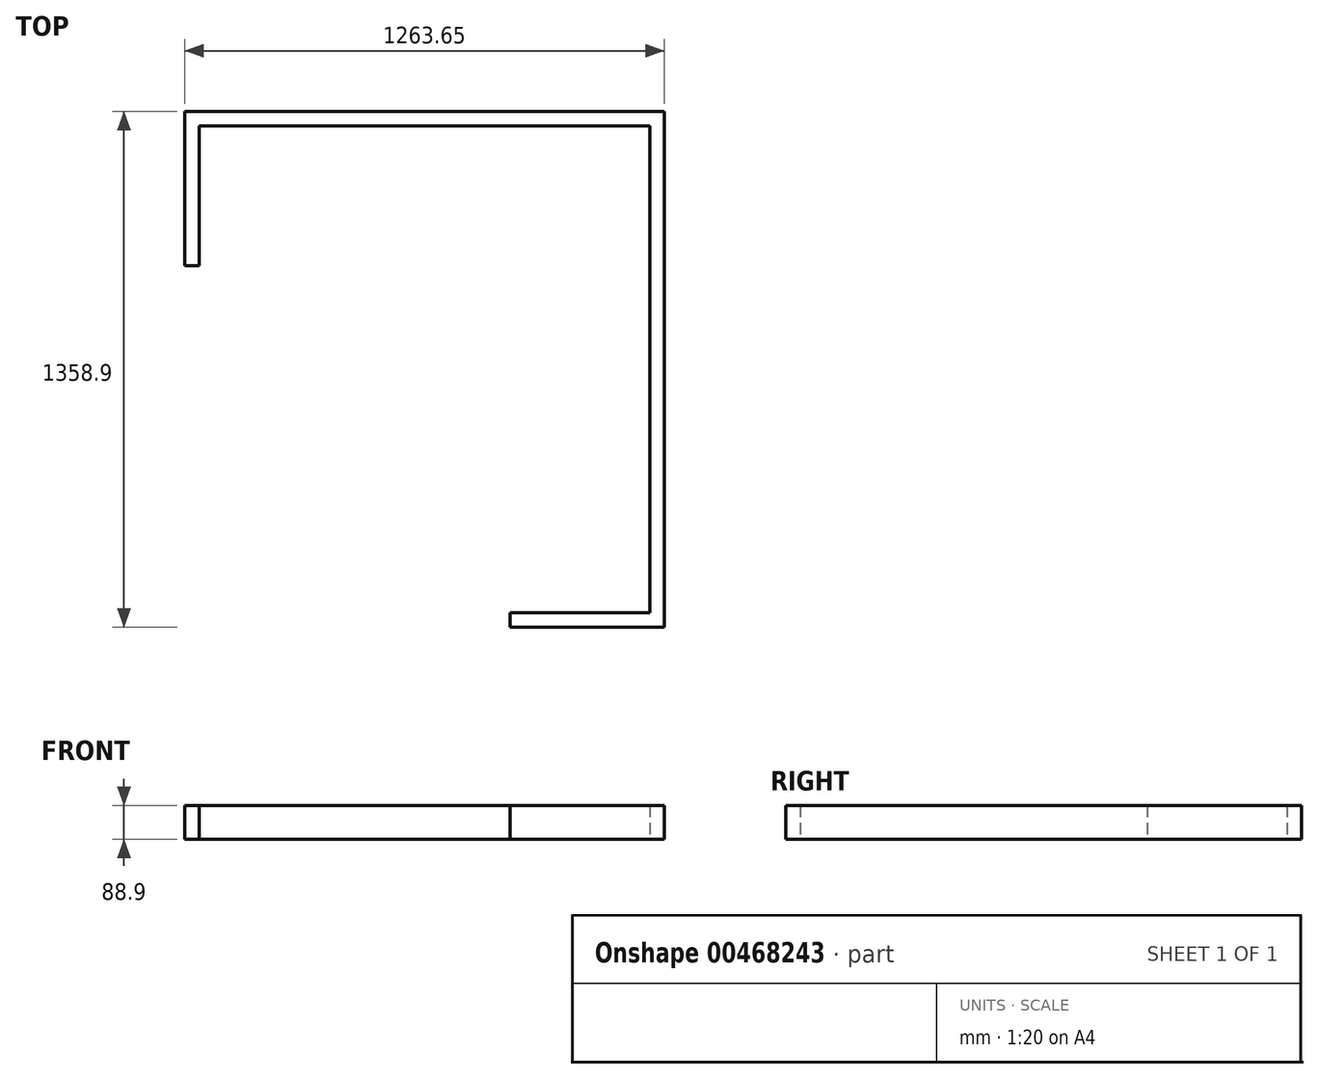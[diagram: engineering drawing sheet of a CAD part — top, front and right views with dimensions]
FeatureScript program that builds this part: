
annotation { "Feature Type Name" : "Feature", "Feature Type Description" : "" }
export const myFeature = defineFeature(function(context is Context, id is Id, definition is map)
    precondition{}
    {
        {
            var Q0;
            Q0=qCreatedBy(makeId("Top.planeOp"),FACE);
            var sketch = newSketch(context, id + "F0", { "sketchPlane" : qUnion([Q0])});
            skLineSegment(sketch, "E0", {"start": v(0, 0) * mm, "end": v(-1263.65, 0) * mm});
            skLineSegment(sketch, "E1", {"start": v(-1263.65, 0) * mm, "end": v(-1263.65, -406.4) * mm});
            skLineSegment(sketch, "E2", {"start": v(-406.4, -1358.9) * mm, "end": v(0, -1358.9) * mm});
            skLineSegment(sketch, "E3", {"start": v(0, -1358.9) * mm, "end": v(0, 0) * mm});
            skLineSegment(sketch, "E4", {"start": v(-1263.65, -406.4) * mm, "end": v(-406.4, -406.4) * mm});
            skLineSegment(sketch, "E5", {"start": v(-406.4, -406.4) * mm, "end": v(-406.4, -1358.9) * mm});
            skLineSegment(sketch, "E6.0", {"start": v(-1225.55, -38.1) * mm, "end": v(-1225.55, -406.4) * mm});
            skLineSegment(sketch, "E6.1", {"start": v(-38.1, -38.1) * mm, "end": v(-1225.55, -38.1) * mm});
            skLineSegment(sketch, "E6.2", {"start": v(-38.1, -1320.8) * mm, "end": v(-38.1, -38.1) * mm});
            skLineSegment(sketch, "E6.3", {"start": v(-406.4, -1320.8) * mm, "end": v(-38.1, -1320.8) * mm});
            skLineSegment(sketch, "E7", {"start": v(-1225.55, -406.4) * mm, "end": v(-1263.65, -406.4) * mm});
            skLineSegment(sketch, "E8", {"start": v(-406.4, -1320.8) * mm, "end": v(-406.4, -1358.9) * mm});
            skSolve(sketch);
        }
        {
            var Q0;
            Q0=makeQuery(id+"F0.imprint","IMPRINT",FACE,{"disambiguationData":[TD([[makeQuery(id+"F0.imprint","IMPRINT",EDGE,{"derivedFrom":sQuery(id+"F0.wireOp",EDGE,"E0")}),1.0]])]});
            extrude(context, id + "F1", {"entities" : qUnion([Q0]), "depth" : 88.9 * mm});
        }
    });
